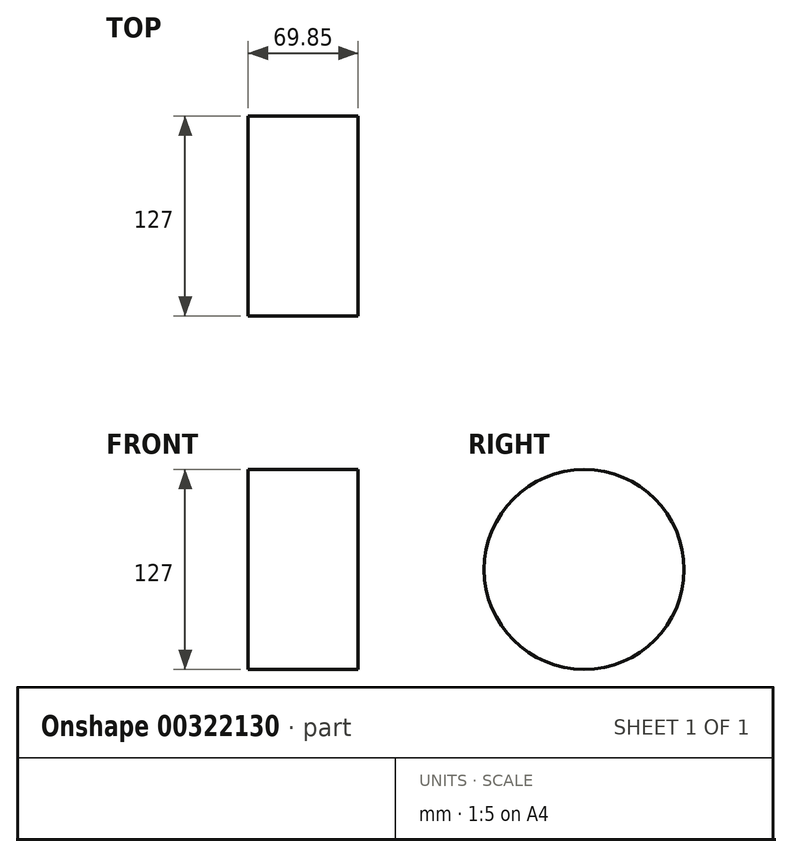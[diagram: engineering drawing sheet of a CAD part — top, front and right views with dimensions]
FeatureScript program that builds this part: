
annotation { "Feature Type Name" : "Feature", "Feature Type Description" : "" }
export const myFeature = defineFeature(function(context is Context, id is Id, definition is map)
    precondition{}
    {
        {
            var Q0;
            Q0=qCreatedBy(makeId("Right.planeOp"),FACE);
            var sketch = newSketch(context, id + "F0", { "sketchPlane" : qUnion([Q0])});
            skCircle(sketch, "E0", {"center": v(0, 0) * mm, "radius": 63.5 * mm});
            skSolve(sketch);
        }
        {
            var Q0;
            Q0=makeQuery(id+"F0.imprint","IMPRINT",FACE,{"disambiguationData":[TD([[makeQuery(id+"F0.imprint","IMPRINT",EDGE,{"derivedFrom":sQuery(id+"F0.wireOp",EDGE,"E0")}),1.0]])]});
            extrude(context, id + "F1", {"entities" : qUnion([Q0]), "depth" : 69.85 * mm});
        }
    });
